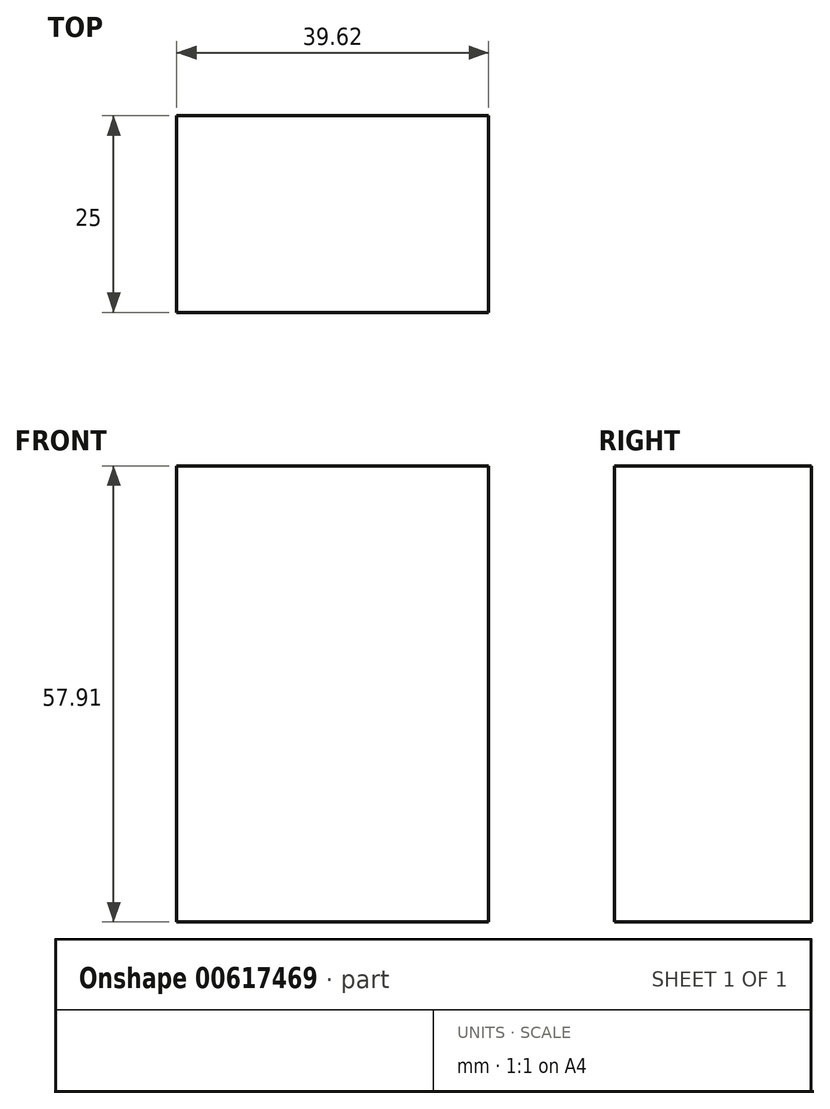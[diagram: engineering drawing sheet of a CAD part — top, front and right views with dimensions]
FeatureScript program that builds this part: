
annotation { "Feature Type Name" : "Feature", "Feature Type Description" : "" }
export const myFeature = defineFeature(function(context is Context, id is Id, definition is map)
    precondition{}
    {
        {
            var Q0;
            Q0=qCreatedBy(makeId("Front.planeOp"),FACE);
            var sketch = newSketch(context, id + "F0", { "sketchPlane" : qUnion([Q0])});
            skLineSegment(sketch, "E0", {"start": v(-37.6, 32.4) * mm, "end": v(-37.6, -25.51) * mm});
            skLineSegment(sketch, "E1", {"start": v(-37.6, -25.51) * mm, "end": v(2.02, -25.51) * mm});
            skLineSegment(sketch, "E2", {"start": v(2.02, -25.51) * mm, "end": v(2.02, 32.4) * mm});
            skLineSegment(sketch, "E3", {"start": v(2.02, 32.4) * mm, "end": v(-37.6, 32.4) * mm});
            skSolve(sketch);
        }
        {
            var Q0;
            Q0 = qSketchRegion(id + "F0", true);
            extrude(context, id + "F1", {"entities" : qUnion([Q0]), "depth" : 25 * mm, "offsetDistance" : 25 * mm});
        }
    });
